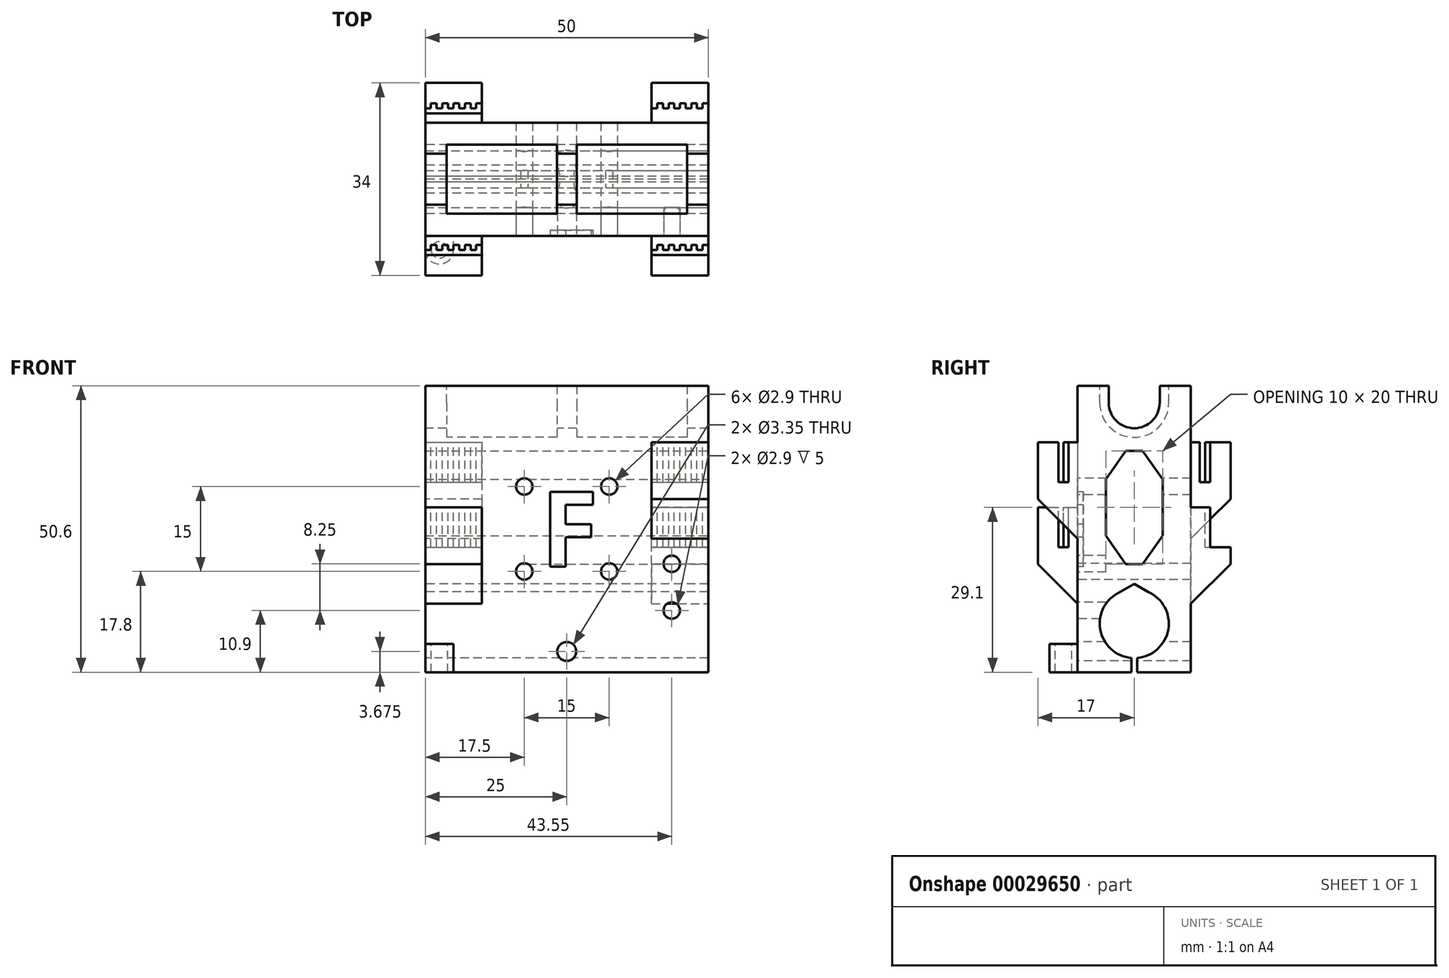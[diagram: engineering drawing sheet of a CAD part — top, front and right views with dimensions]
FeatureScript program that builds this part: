
annotation { "Feature Type Name" : "Feature", "Feature Type Description" : "" }
export const myFeature = defineFeature(function(context is Context, id is Id, definition is map)
    precondition{}
    {
        {
            var Q0;
            Q0=qCreatedBy(makeId("Top.planeOp"),FACE);
            var sketch = newSketch(context, id + "F0", { "sketchPlane" : qUnion([Q0])});
            skLineSegment(sketch, "E0.bottom", {"start": v(0, 0) * mm, "end": v(50, 0) * mm});
            skLineSegment(sketch, "E0.top", {"start": v(0, 20) * mm, "end": v(50, 20) * mm});
            skLineSegment(sketch, "E0.left", {"start": v(0, 0) * mm, "end": v(0, 20) * mm});
            skLineSegment(sketch, "E0.right", {"start": v(50, 0) * mm, "end": v(50, 20) * mm});
            skSolve(sketch);
        }
        {
            var Q0;
            Q0=qSketchRegion(id+"F0",true);
            extrude(context, id + "F1", {"entities" : qUnion([Q0]), "depth" : 50.6 * mm});
        }
        {
            var Q0;
            Q0=makeQuery(id+"F1.opExtrude","SWEPT_FACE",FACE,{"disambiguationData":[OSD([sQuery(id+"F0.wireOp",EDGE,"E0.left")])]});
            var sketch = newSketch(context, id + "F2", { "sketchPlane" : qUnion([Q0])});
            skCircle(sketch, "E1", {"center": v(-10, 8.6) * mm, "radius": 6.1 * mm});
            skCircle(sketch, "E2", {"center": v(-10, 47.6) * mm, "radius": 4.5 * mm});
            skLineSegment(sketch, "E3", {"start": v(-20, 47.6) * mm, "end": v(0, 47.6) * mm, "construction": true});
            skLineSegment(sketch, "E4", {"start": v(-14.5, 50.6) * mm, "end": v(-14.5, 47.6) * mm});
            skLineSegment(sketch, "E5", {"start": v(-5.5, 50.6) * mm, "end": v(-5.5, 47.6) * mm});
            skLineSegment(sketch, "E6", {"start": v(-20, 8.6) * mm, "end": v(0, 8.6) * mm, "construction": true});
            skLineSegment(sketch, "E7", {"start": v(-10, 8.6) * mm, "end": v(-10, 0) * mm, "construction": true});
            skLineSegment(sketch, "E8", {"start": v(-10, 0) * mm, "end": v(-10.5, 0) * mm});
            skLineSegment(sketch, "E9", {"start": v(-10.5, 0) * mm, "end": v(-10.5, 2.52) * mm});
            skLineSegment(sketch, "E10", {"start": v(-10.5, 2.52) * mm, "end": v(-9.5, 2.52) * mm});
            skLineSegment(sketch, "E11", {"start": v(-9.5, 2.52) * mm, "end": v(-9.5, 0) * mm});
            skLineSegment(sketch, "E12", {"start": v(-9.5, 0) * mm, "end": v(-10, 0) * mm});
            skLineSegment(sketch, "E13", {"start": v(-10, 14.7) * mm, "end": v(-10, 15.6) * mm});
            skLineSegment(sketch, "E14", {"start": v(-10, 15.6) * mm, "end": v(-6.39, 13.51) * mm});
            skLineSegment(sketch, "E15", {"start": v(-10, 15.6) * mm, "end": v(-13.61, 13.51) * mm});
            skCircle(sketch, "E16", {"center": v(-10, 47.6) * mm, "radius": 6.1 * mm});
            skLineSegment(sketch, "E17", {"start": v(-3.9, 47.6) * mm, "end": v(-3.9, 50.6) * mm});
            skLineSegment(sketch, "E18", {"start": v(-16.1, 47.6) * mm, "end": v(-16.1, 50.6) * mm});
            skSolve(sketch);
        }
        {
            var Q0;
            {var subQ0=sQuery(id+"F2.wireOp",EDGE,"E14");var subQ1=sQuery(id+"F2.wireOp",EDGE,"E1");var subQ3=makeQuery(id+"F2.imprint","INTERSECT",VERTEX,{"disambiguationData":[OD(0.0)],"derivedFrom":[subQ1,subQ0]});Q0=makeQuery(id+"F2.imprint","IMPRINT",FACE,{"disambiguationData":[TD([[makeQuery(id+"F2.imprint","IMPRINT",EDGE,{"disambiguationData":[TD([[subQ3,-1.0]])],"derivedFrom":subQ1}),1.0]])]});}
            var Q1;
            {var subQ0=sQuery(id+"F2.wireOp",EDGE,"E15");var subQ1=sQuery(id+"F2.wireOp",EDGE,"E1");var subQ3=makeQuery(id+"F2.imprint","INTERSECT",VERTEX,{"disambiguationData":[OD(0.0)],"derivedFrom":[subQ1,subQ0]});Q1=makeQuery(id+"F2.imprint","IMPRINT",FACE,{"disambiguationData":[TD([[makeQuery(id+"F2.imprint","IMPRINT",EDGE,{"disambiguationData":[TD([[subQ3,1.0]])],"derivedFrom":subQ1}),1.0]])]});}
            var Q2;
            Q2=makeQuery(id+"F2.imprint","IMPRINT",FACE,{"disambiguationData":[TD([[makeQuery(id+"F2.imprint","IMPRINT",EDGE,{"derivedFrom":sQuery(id+"F2.wireOp",EDGE,"E8")}),-1.0]])]});
            var Q3;
            {var subQ0=sQuery(id+"F2.wireOp",EDGE,"E10");Q3=makeQuery(id+"F2.imprint","IMPRINT",FACE,{"disambiguationData":[TD([[makeQuery(id+"F2.imprint","IMPRINT",EDGE,{"derivedFrom":subQ0}),-1.0]])]});}
            var Q4;
            {var subQ3=sQuery(id+"F2.wireOp",EDGE,"E13");Q4=makeQuery(id+"F2.imprint","IMPRINT",FACE,{"disambiguationData":[TD([[makeQuery(id+"F2.imprint","IMPRINT",EDGE,{"derivedFrom":subQ3}),-1.0]])]});}
            var Q5;
            {var subQ3=sQuery(id+"F2.wireOp",EDGE,"E13");Q5=makeQuery(id+"F2.imprint","IMPRINT",FACE,{"disambiguationData":[TD([[makeQuery(id+"F2.imprint","IMPRINT",EDGE,{"derivedFrom":subQ3}),1.0]])]});}
            var Q6;
            {var subQ7=sQuery(id+"F2.wireOp",EDGE,"E10");Q6=makeQuery(id+"F2.imprint","IMPRINT",FACE,{"disambiguationData":[TD([[makeQuery(id+"F2.imprint","IMPRINT",EDGE,{"derivedFrom":subQ7}),1.0]])]});}
            var Q7;
            {var subQ3=sQuery(id+"F2.wireOp",EDGE,"E5");Q7=makeQuery(id+"F2.imprint","IMPRINT",FACE,{"disambiguationData":[TD([[makeQuery(id+"F2.imprint","IMPRINT",EDGE,{"derivedFrom":subQ3}),-1.0]])]});}
            var Q8;
            {var subQ0=sQuery(id+"F2.wireOp",EDGE,"E4");Q8=makeQuery(id+"F2.imprint","IMPRINT",FACE,{"disambiguationData":[TD([[makeQuery(id+"F2.imprint","IMPRINT",EDGE,{"derivedFrom":subQ0}),1.0]])]});}
            var Q9;
            {var subQ0=sQuery(id+"F2.wireOp",EDGE,"E4");Q9=makeQuery(id+"F2.imprint","IMPRINT",FACE,{"disambiguationData":[TD([[makeQuery(id+"F2.imprint","IMPRINT",EDGE,{"derivedFrom":subQ0}),1.0]])]});}
            var Q10;
            {var subQ3=sQuery(id+"F2.wireOp",EDGE,"E5");Q10=makeQuery(id+"F2.imprint","IMPRINT",FACE,{"disambiguationData":[TD([[makeQuery(id+"F2.imprint","IMPRINT",EDGE,{"derivedFrom":subQ3}),-1.0]])]});}
            var Q11;
            {var subQ1=sQuery(id+"F2.wireOp",EDGE,"E2");var subQ4=makeQuery(id+"F2.imprint","INTERSECT",VERTEX,{"derivedFrom":[subQ1,sQuery(id+"F2.wireOp",EDGE,"E5")]});Q11=makeQuery(id+"F2.imprint","IMPRINT",FACE,{"disambiguationData":[TD([[makeQuery(id+"F2.imprint","IMPRINT",EDGE,{"disambiguationData":[TD([[subQ4,-1.0]])],"derivedFrom":subQ1}),1.0]])]});}
            extrude(context, id + "F3", {"entities" : qUnion([Q0, Q1, Q2, Q3, Q4, Q5, Q6, Q7, Q8, Q9, Q10, Q11]), "operationType" : NewBodyOperationType.REMOVE, "endBound" : BoundingType.THROUGH_ALL, "oppositeDirection" : true, "depth" : 25 * mm});
        }
        {
            var Q0;
            {var subQ3=sQuery(id+"F2.wireOp",EDGE,"E4");Q0=makeQuery(id+"F2.imprint","IMPRINT",FACE,{"disambiguationData":[TD([[makeQuery(id+"F2.imprint","IMPRINT",EDGE,{"derivedFrom":subQ3}),-1.0]])]});}
            var Q1;
            {var subQ3=sQuery(id+"F2.wireOp",EDGE,"E18");Q1=makeQuery(id+"F2.imprint","IMPRINT",FACE,{"disambiguationData":[TD([[makeQuery(id+"F2.imprint","IMPRINT",EDGE,{"derivedFrom":subQ3}),-1.0]])]});}
            var Q2;
            {var subQ3=sQuery(id+"F2.wireOp",EDGE,"E17");Q2=makeQuery(id+"F2.imprint","IMPRINT",FACE,{"disambiguationData":[TD([[makeQuery(id+"F2.imprint","IMPRINT",EDGE,{"derivedFrom":subQ3}),1.0]])]});}
            extrude(context, id + "F4", {"entities" : qUnion([Q0, Q1, Q2]), "operationType" : NewBodyOperationType.REMOVE, "oppositeDirection" : true, "depth" : 46.25 * mm});
        }
        {
            var Q0;
            {var subQ3=sQuery(id+"F2.wireOp",EDGE,"E4");Q0=makeQuery(id+"F2.imprint","IMPRINT",FACE,{"disambiguationData":[TD([[makeQuery(id+"F2.imprint","IMPRINT",EDGE,{"derivedFrom":subQ3}),-1.0]])]});}
            var Q1;
            {var subQ3=sQuery(id+"F2.wireOp",EDGE,"E18");Q1=makeQuery(id+"F2.imprint","IMPRINT",FACE,{"disambiguationData":[TD([[makeQuery(id+"F2.imprint","IMPRINT",EDGE,{"derivedFrom":subQ3}),-1.0]])]});}
            var Q2;
            {var subQ3=sQuery(id+"F2.wireOp",EDGE,"E17");Q2=makeQuery(id+"F2.imprint","IMPRINT",FACE,{"disambiguationData":[TD([[makeQuery(id+"F2.imprint","IMPRINT",EDGE,{"derivedFrom":subQ3}),1.0]])]});}
            extrude(context, id + "F5", {"entities" : qUnion([Q0, Q1, Q2]), "operationType" : NewBodyOperationType.ADD, "oppositeDirection" : true, "depth" : 26.75 * mm});
        }
        {
            var Q0;
            {var subQ3=sQuery(id+"F2.wireOp",EDGE,"E4");Q0=makeQuery(id+"F2.imprint","IMPRINT",FACE,{"disambiguationData":[TD([[makeQuery(id+"F2.imprint","IMPRINT",EDGE,{"derivedFrom":subQ3}),-1.0]])]});}
            var Q1;
            {var subQ3=sQuery(id+"F2.wireOp",EDGE,"E18");Q1=makeQuery(id+"F2.imprint","IMPRINT",FACE,{"disambiguationData":[TD([[makeQuery(id+"F2.imprint","IMPRINT",EDGE,{"derivedFrom":subQ3}),-1.0]])]});}
            var Q2;
            {var subQ3=sQuery(id+"F2.wireOp",EDGE,"E17");Q2=makeQuery(id+"F2.imprint","IMPRINT",FACE,{"disambiguationData":[TD([[makeQuery(id+"F2.imprint","IMPRINT",EDGE,{"derivedFrom":subQ3}),1.0]])]});}
            extrude(context, id + "F6", {"entities" : qUnion([Q0, Q1, Q2]), "operationType" : NewBodyOperationType.REMOVE, "oppositeDirection" : true, "depth" : 23.25 * mm});
        }
        {
            var Q0;
            {var subQ3=sQuery(id+"F2.wireOp",EDGE,"E4");Q0=makeQuery(id+"F2.imprint","IMPRINT",FACE,{"disambiguationData":[TD([[makeQuery(id+"F2.imprint","IMPRINT",EDGE,{"derivedFrom":subQ3}),-1.0]])]});}
            var Q1;
            {var subQ3=sQuery(id+"F2.wireOp",EDGE,"E18");Q1=makeQuery(id+"F2.imprint","IMPRINT",FACE,{"disambiguationData":[TD([[makeQuery(id+"F2.imprint","IMPRINT",EDGE,{"derivedFrom":subQ3}),-1.0]])]});}
            var Q2;
            {var subQ3=sQuery(id+"F2.wireOp",EDGE,"E17");Q2=makeQuery(id+"F2.imprint","IMPRINT",FACE,{"disambiguationData":[TD([[makeQuery(id+"F2.imprint","IMPRINT",EDGE,{"derivedFrom":subQ3}),1.0]])]});}
            extrude(context, id + "F7", {"entities" : qUnion([Q0, Q1, Q2]), "operationType" : NewBodyOperationType.ADD, "oppositeDirection" : true, "depth" : 3.75 * mm});
        }
        {
            var Q0;
            Q0=makeQuery(id+"F1.opExtrude","SWEPT_FACE",FACE,{"disambiguationData":[OSD([sQuery(id+"F0.wireOp",EDGE,"E0.bottom")])]});
            var sketch = newSketch(context, id + "F8", { "sketchPlane" : qUnion([Q0])});
            skLineSegment(sketch, "E19.bottom", {"start": v(0, 29.1) * mm, "end": v(10, 29.1) * mm});
            skLineSegment(sketch, "E19.top", {"start": v(0, 9.1) * mm, "end": v(10, 9.1) * mm});
            skLineSegment(sketch, "E19.left", {"start": v(0, 29.1) * mm, "end": v(0, 9.1) * mm});
            skLineSegment(sketch, "E19.right", {"start": v(10, 29.1) * mm, "end": v(10, 9.1) * mm});
            skLineSegment(sketch, "E20.bottom", {"start": v(50, 40.6) * mm, "end": v(40, 40.6) * mm});
            skLineSegment(sketch, "E20.top", {"start": v(50, 20.6) * mm, "end": v(40, 20.6) * mm});
            skLineSegment(sketch, "E20.left", {"start": v(50, 40.6) * mm, "end": v(50, 20.6) * mm});
            skLineSegment(sketch, "E20.right", {"start": v(40, 40.6) * mm, "end": v(40, 20.6) * mm});
            skPoint(sketch, "E21", {"position": v(0, 47.6) * mm});
            skPoint(sketch, "E22", {"position": v(0, 8.6) * mm});
            skSolve(sketch);
        }
        {
            var Q0;
            Q0=qSketchRegion(id+"F8",true);
            extrude(context, id + "F9", {"entities" : qUnion([Q0]), "operationType" : NewBodyOperationType.ADD, "depth" : 7 * mm});
        }
        {
            var Q0;
            Q0=makeQuery(id+"F9.opExtrude","CAP_EDGE",EDGE,{"disambiguationData":[OSD([sQuery(id+"F8.wireOp",EDGE,"E19.top")])],"isStart":false});
            var Q1;
            Q1=makeQuery(id+"F9.opExtrude","CAP_EDGE",EDGE,{"disambiguationData":[OSD([sQuery(id+"F8.wireOp",EDGE,"E20.top")])],"isStart":false});
            chamfer(context, id + "F10", {"entities" : qUnion([Q0, Q1]), "width" : 10 * mm, "tangentPropagation" : true});
        }
        {
            var Q0;
            Q0=makeQuery(id+"F9.opExtrude","SWEPT_FACE",FACE,{"disambiguationData":[OSD([sQuery(id+"F8.wireOp",EDGE,"E19.bottom")])]});
            var sketch = newSketch(context, id + "F11", { "sketchPlane" : qUnion([Q0])});
            skLineSegment(sketch, "E23", {"start": v(-935.9, 0) * mm, "end": v(-935.88, -4.54) * mm});
            skLineSegment(sketch, "E24.left", {"start": v(0, -3.4) * mm, "end": v(0, -1.6) * mm});
            skLineSegment(sketch, "E25", {"start": v(6, -2.5) * mm, "end": v(7, -2.5) * mm});
            skLineSegment(sketch, "E26", {"start": v(4, -2.5) * mm, "end": v(5, -2.5) * mm});
            skLineSegment(sketch, "E27", {"start": v(0, -2.5) * mm, "end": v(1, -2.5) * mm});
            skLineSegment(sketch, "E28", {"start": v(7, -1.6) * mm, "end": v(8, -1.6) * mm});
            skLineSegment(sketch, "E29", {"start": v(2, -2.5) * mm, "end": v(3, -2.5) * mm});
            skLineSegment(sketch, "E30", {"start": v(3, -1.6) * mm, "end": v(4, -1.6) * mm});
            skLineSegment(sketch, "E31", {"start": v(8, -2.5) * mm, "end": v(9, -2.5) * mm});
            skLineSegment(sketch, "E32", {"start": v(8, -1.6) * mm, "end": v(8, -2.5) * mm});
            skLineSegment(sketch, "E33", {"start": v(9, -2.5) * mm, "end": v(9, -1.6) * mm});
            skLineSegment(sketch, "E34", {"start": v(10, -1.6) * mm, "end": v(10, -2.5) * mm});
            skLineSegment(sketch, "E35", {"start": v(6, -1.6) * mm, "end": v(6, -2.5) * mm});
            skLineSegment(sketch, "E36", {"start": v(2, -1.6) * mm, "end": v(2, -2.5) * mm});
            skLineSegment(sketch, "E37", {"start": v(1, -1.6) * mm, "end": v(2, -1.6) * mm});
            skLineSegment(sketch, "E38", {"start": v(1, -2.5) * mm, "end": v(1, -1.6) * mm});
            skLineSegment(sketch, "E39", {"start": v(9, -1.6) * mm, "end": v(10, -1.6) * mm});
            skLineSegment(sketch, "E40", {"start": v(5, -1.6) * mm, "end": v(6, -1.6) * mm});
            skLineSegment(sketch, "E41", {"start": v(5, -2.5) * mm, "end": v(5, -1.6) * mm});
            skLineSegment(sketch, "E42", {"start": v(3, -2.5) * mm, "end": v(3, -1.6) * mm});
            skLineSegment(sketch, "E43", {"start": v(4, -1.6) * mm, "end": v(4, -2.5) * mm});
            skLineSegment(sketch, "E44", {"start": v(7, -2.5) * mm, "end": v(7, -1.6) * mm});
            skLineSegment(sketch, "E45", {"start": v(0, -1.6) * mm, "end": v(0, -2.5) * mm});
            skLineSegment(sketch, "E46", {"start": v(10, -2.5) * mm, "end": v(10, -3.4) * mm});
            skLineSegment(sketch, "E47", {"start": v(0, -3.4) * mm, "end": v(10, -3.4) * mm});
            skLineSegment(sketch, "E48", {"start": v(5.3, -1.6) * mm, "end": v(5.3, 0) * mm});
            skSolve(sketch);
        }
        {
            var Q0;
            Q0=qSketchRegion(id+"F11",true);
            extrude(context, id + "F12", {"entities" : qUnion([Q0]), "operationType" : NewBodyOperationType.REMOVE, "oppositeDirection" : true, "depth" : 7 * mm});
        }
        {
            var Q0;
            Q0=makeQuery(id+"F9.opExtrude","SWEPT_FACE",FACE,{"disambiguationData":[OSD([sQuery(id+"F8.wireOp",EDGE,"E20.bottom")])]});
            var sketch = newSketch(context, id + "F13", { "sketchPlane" : qUnion([Q0])});
            skLineSegment(sketch, "E49.left", {"start": v(40, -3.4) * mm, "end": v(40, -1.6) * mm});
            skLineSegment(sketch, "E50", {"start": v(46, -2.5) * mm, "end": v(47, -2.5) * mm});
            skLineSegment(sketch, "E51", {"start": v(44, -2.5) * mm, "end": v(45, -2.5) * mm});
            skLineSegment(sketch, "E52", {"start": v(40, -2.5) * mm, "end": v(41, -2.5) * mm});
            skLineSegment(sketch, "E53", {"start": v(47, -1.6) * mm, "end": v(48, -1.6) * mm});
            skLineSegment(sketch, "E54", {"start": v(42, -2.5) * mm, "end": v(43, -2.5) * mm});
            skLineSegment(sketch, "E55", {"start": v(43, -1.6) * mm, "end": v(44, -1.6) * mm});
            skLineSegment(sketch, "E56", {"start": v(48, -2.5) * mm, "end": v(49, -2.5) * mm});
            skLineSegment(sketch, "E57", {"start": v(48, -1.6) * mm, "end": v(48, -2.5) * mm});
            skLineSegment(sketch, "E58", {"start": v(49, -2.5) * mm, "end": v(49, -1.6) * mm});
            skLineSegment(sketch, "E59", {"start": v(50, -1.6) * mm, "end": v(50, -2.5) * mm});
            skLineSegment(sketch, "E60", {"start": v(46, -1.6) * mm, "end": v(46, -2.5) * mm});
            skLineSegment(sketch, "E61", {"start": v(42, -1.6) * mm, "end": v(42, -2.5) * mm});
            skLineSegment(sketch, "E62", {"start": v(41, -1.6) * mm, "end": v(42, -1.6) * mm});
            skLineSegment(sketch, "E63", {"start": v(41, -2.5) * mm, "end": v(41, -1.6) * mm});
            skLineSegment(sketch, "E64", {"start": v(49, -1.6) * mm, "end": v(50, -1.6) * mm});
            skLineSegment(sketch, "E65", {"start": v(45, -1.6) * mm, "end": v(46, -1.6) * mm});
            skLineSegment(sketch, "E66", {"start": v(45, -2.5) * mm, "end": v(45, -1.6) * mm});
            skLineSegment(sketch, "E67", {"start": v(43, -2.5) * mm, "end": v(43, -1.6) * mm});
            skLineSegment(sketch, "E68", {"start": v(44, -1.6) * mm, "end": v(44, -2.5) * mm});
            skLineSegment(sketch, "E69", {"start": v(47, -2.5) * mm, "end": v(47, -1.6) * mm});
            skLineSegment(sketch, "E70", {"start": v(40, -1.6) * mm, "end": v(40, -2.5) * mm});
            skLineSegment(sketch, "E71", {"start": v(50, -2.5) * mm, "end": v(50, -3.4) * mm});
            skLineSegment(sketch, "E72", {"start": v(40, -3.4) * mm, "end": v(50, -3.4) * mm});
            skLineSegment(sketch, "E73", {"start": v(45.23, -1.6) * mm, "end": v(45.23, 0) * mm});
            skSolve(sketch);
        }
        {
            var Q0;
            Q0=qSketchRegion(id+"F13",true);
            extrude(context, id + "F14", {"entities" : qUnion([Q0]), "operationType" : NewBodyOperationType.REMOVE, "oppositeDirection" : true, "depth" : 7 * mm});
        }
        {
            var Q0;
            Q0=makeQuery(id+"F1.opExtrude","SWEPT_FACE",FACE,{"disambiguationData":[OSD([sQuery(id+"F0.wireOp",EDGE,"E0.top")])]});
            var sketch = newSketch(context, id + "F15", { "sketchPlane" : qUnion([Q0])});
            skLineSegment(sketch, "E74.bottom", {"start": v(-50, 9.1) * mm, "end": v(-40, 9.1) * mm});
            skLineSegment(sketch, "E74.top", {"start": v(-50, 29.1) * mm, "end": v(-40, 29.1) * mm});
            skLineSegment(sketch, "E74.left", {"start": v(-50, 9.1) * mm, "end": v(-50, 29.1) * mm});
            skLineSegment(sketch, "E74.right", {"start": v(-40, 9.1) * mm, "end": v(-40, 29.1) * mm});
            skLineSegment(sketch, "E75.bottom", {"start": v(0, 40.6) * mm, "end": v(-10, 40.6) * mm});
            skLineSegment(sketch, "E75.top", {"start": v(0, 20.6) * mm, "end": v(-10, 20.6) * mm});
            skLineSegment(sketch, "E75.left", {"start": v(0, 40.6) * mm, "end": v(0, 20.6) * mm});
            skLineSegment(sketch, "E75.right", {"start": v(-10, 40.6) * mm, "end": v(-10, 20.6) * mm});
            skSolve(sketch);
        }
        {
            var Q0;
            Q0=qSketchRegion(id+"F15",true);
            extrude(context, id + "F16", {"entities" : qUnion([Q0]), "operationType" : NewBodyOperationType.ADD, "depth" : 7 * mm});
        }
        {
            var Q0;
            Q0=makeQuery(id+"F16.opExtrude","SWEPT_FACE",FACE,{"disambiguationData":[OSD([sQuery(id+"F15.wireOp",EDGE,"E74.top")])]});
            var sketch = newSketch(context, id + "F17", { "sketchPlane" : qUnion([Q0])});
            skLineSegment(sketch, "E76.left", {"start": v(40, 21.6) * mm, "end": v(40, 23.4) * mm});
            skLineSegment(sketch, "E77", {"start": v(46, 22.5) * mm, "end": v(47, 22.5) * mm});
            skLineSegment(sketch, "E78", {"start": v(44, 22.5) * mm, "end": v(45, 22.5) * mm});
            skLineSegment(sketch, "E79", {"start": v(40, 22.5) * mm, "end": v(41, 22.5) * mm});
            skLineSegment(sketch, "E80", {"start": v(47, 23.4) * mm, "end": v(48, 23.4) * mm});
            skLineSegment(sketch, "E81", {"start": v(42, 22.5) * mm, "end": v(43, 22.5) * mm});
            skLineSegment(sketch, "E82", {"start": v(43, 23.4) * mm, "end": v(44, 23.4) * mm});
            skLineSegment(sketch, "E83", {"start": v(48, 22.5) * mm, "end": v(49, 22.5) * mm});
            skLineSegment(sketch, "E84", {"start": v(48, 23.4) * mm, "end": v(48, 22.5) * mm});
            skLineSegment(sketch, "E85", {"start": v(49, 22.5) * mm, "end": v(49, 23.4) * mm});
            skLineSegment(sketch, "E86", {"start": v(50, 23.4) * mm, "end": v(50, 22.5) * mm});
            skLineSegment(sketch, "E87", {"start": v(46, 23.4) * mm, "end": v(46, 22.5) * mm});
            skLineSegment(sketch, "E88", {"start": v(42, 23.4) * mm, "end": v(42, 22.5) * mm});
            skLineSegment(sketch, "E89", {"start": v(41, 23.4) * mm, "end": v(42, 23.4) * mm});
            skLineSegment(sketch, "E90", {"start": v(41, 22.5) * mm, "end": v(41, 23.4) * mm});
            skLineSegment(sketch, "E91", {"start": v(49, 23.4) * mm, "end": v(50, 23.4) * mm});
            skLineSegment(sketch, "E92", {"start": v(45, 23.4) * mm, "end": v(46, 23.4) * mm});
            skLineSegment(sketch, "E93", {"start": v(45, 22.5) * mm, "end": v(45, 23.4) * mm});
            skLineSegment(sketch, "E94", {"start": v(43, 22.5) * mm, "end": v(43, 23.4) * mm});
            skLineSegment(sketch, "E95", {"start": v(44, 23.4) * mm, "end": v(44, 22.5) * mm});
            skLineSegment(sketch, "E96", {"start": v(47, 22.5) * mm, "end": v(47, 23.4) * mm});
            skLineSegment(sketch, "E97", {"start": v(40, 23.4) * mm, "end": v(40, 22.5) * mm});
            skLineSegment(sketch, "E98", {"start": v(50, 22.5) * mm, "end": v(50, 21.6) * mm});
            skLineSegment(sketch, "E99", {"start": v(40, 21.6) * mm, "end": v(50, 21.6) * mm});
            skLineSegment(sketch, "E100", {"start": v(45, 21.6) * mm, "end": v(45, 20) * mm});
            skSolve(sketch);
        }
        {
            var Q0;
            {var subQ4=sQuery(id+"F17.wireOp",EDGE,"E76.left");Q0=makeQuery(id+"F17.imprint","IMPRINT",FACE,{"disambiguationData":[TD([[makeQuery(id+"F17.imprint","IMPRINT",EDGE,{"derivedFrom":subQ4}),1.0]])]});}
            extrude(context, id + "F18", {"entities" : qUnion([Q0]), "operationType" : NewBodyOperationType.REMOVE, "oppositeDirection" : true, "depth" : 7 * mm});
        }
        {
            var Q0;
            Q0=makeQuery(id+"F16.opExtrude","SWEPT_FACE",FACE,{"disambiguationData":[OSD([sQuery(id+"F15.wireOp",EDGE,"E75.bottom")])]});
            var sketch = newSketch(context, id + "F19", { "sketchPlane" : qUnion([Q0])});
            skLineSegment(sketch, "E101", {"start": v(6, 22.5) * mm, "end": v(7, 22.5) * mm});
            skLineSegment(sketch, "E102", {"start": v(4, 22.5) * mm, "end": v(5, 22.5) * mm});
            skLineSegment(sketch, "E103", {"start": v(0, 22.5) * mm, "end": v(1, 22.5) * mm});
            skLineSegment(sketch, "E104", {"start": v(7, 23.4) * mm, "end": v(8, 23.4) * mm});
            skLineSegment(sketch, "E105", {"start": v(2, 22.5) * mm, "end": v(3, 22.5) * mm});
            skLineSegment(sketch, "E106", {"start": v(3, 23.4) * mm, "end": v(4, 23.4) * mm});
            skLineSegment(sketch, "E107", {"start": v(8, 22.5) * mm, "end": v(9, 22.5) * mm});
            skLineSegment(sketch, "E108", {"start": v(8, 23.4) * mm, "end": v(8, 22.5) * mm});
            skLineSegment(sketch, "E109", {"start": v(9, 22.5) * mm, "end": v(9, 23.4) * mm});
            skLineSegment(sketch, "E110", {"start": v(10, 23.4) * mm, "end": v(10, 22.5) * mm});
            skLineSegment(sketch, "E111", {"start": v(6, 23.4) * mm, "end": v(6, 22.5) * mm});
            skLineSegment(sketch, "E112", {"start": v(2, 23.4) * mm, "end": v(2, 22.5) * mm});
            skLineSegment(sketch, "E113", {"start": v(1, 23.4) * mm, "end": v(2, 23.4) * mm});
            skLineSegment(sketch, "E114", {"start": v(1, 22.5) * mm, "end": v(1, 23.4) * mm});
            skLineSegment(sketch, "E115", {"start": v(9, 23.4) * mm, "end": v(10, 23.4) * mm});
            skLineSegment(sketch, "E116", {"start": v(5, 23.4) * mm, "end": v(6, 23.4) * mm});
            skLineSegment(sketch, "E117", {"start": v(5, 22.5) * mm, "end": v(5, 23.4) * mm});
            skLineSegment(sketch, "E118", {"start": v(3, 22.5) * mm, "end": v(3, 23.4) * mm});
            skLineSegment(sketch, "E119", {"start": v(4, 23.4) * mm, "end": v(4, 22.5) * mm});
            skLineSegment(sketch, "E120", {"start": v(7, 22.5) * mm, "end": v(7, 23.4) * mm});
            skLineSegment(sketch, "E121", {"start": v(10, 22.5) * mm, "end": v(10, 21.6) * mm});
            skLineSegment(sketch, "E122", {"start": v(0, 21.6) * mm, "end": v(10, 21.6) * mm});
            skLineSegment(sketch, "E123", {"start": v(5, 21.6) * mm, "end": v(5, 20) * mm});
            skLineSegment(sketch, "E124", {"start": v(0, 21.6) * mm, "end": v(0, 22.5) * mm});
            skSolve(sketch);
        }
        {
            var Q0;
            Q0=makeQuery(id+"F19.imprint","IMPRINT",FACE,{"disambiguationData":[TD([[makeQuery(id+"F19.imprint","IMPRINT",EDGE,{"derivedFrom":sQuery(id+"F19.wireOp",EDGE,"E101")}),-1.0]])]});
            extrude(context, id + "F20", {"entities" : qUnion([Q0]), "operationType" : NewBodyOperationType.REMOVE, "oppositeDirection" : true, "depth" : 7 * mm});
        }
        {
            var Q0;
            Q0=makeQuery(id+"F16.opExtrude","CAP_EDGE",EDGE,{"disambiguationData":[OSD([sQuery(id+"F15.wireOp",EDGE,"E75.top")])],"isStart":false});
            var Q1;
            Q1=makeQuery(id+"F16.opExtrude","CAP_EDGE",EDGE,{"disambiguationData":[OSD([sQuery(id+"F15.wireOp",EDGE,"E74.bottom")])],"isStart":false});
            chamfer(context, id + "F21", {"entities" : qUnion([Q0, Q1]), "width" : 10 * mm, "tangentPropagation" : true});
        }
        {
            var Q0;
            Q0=makeQuery(id+"F1.opExtrude","SWEPT_FACE",FACE,{"disambiguationData":[OSD([sQuery(id+"F0.wireOp",EDGE,"E0.bottom")])]});
            var sketch = newSketch(context, id + "F22", { "sketchPlane" : qUnion([Q0])});
            skCircle(sketch, "E125", {"center": v(17.5, 32.8) * mm, "radius": 1.45 * mm});
            skCircle(sketch, "E126", {"center": v(32.5, 32.8) * mm, "radius": 1.45 * mm});
            skCircle(sketch, "E127", {"center": v(17.5, 17.8) * mm, "radius": 1.45 * mm});
            skCircle(sketch, "E128", {"center": v(32.5, 17.8) * mm, "radius": 1.45 * mm});
            skLineSegment(sketch, "E129", {"start": v(17.5, 32.8) * mm, "end": v(0, 32.8) * mm});
            skLineSegment(sketch, "E130", {"start": v(32.5, 17.8) * mm, "end": v(50, 17.8) * mm});
            skLineSegment(sketch, "E131", {"start": v(32.5, 32.8) * mm, "end": v(32.5, 50.6) * mm});
            skLineSegment(sketch, "E132", {"start": v(17.5, 17.8) * mm, "end": v(17.5, 0) * mm});
            skCircle(sketch, "E133", {"center": v(25, 3.68) * mm, "radius": 1.68 * mm});
            skLineSegment(sketch, "E134", {"start": v(25, 0) * mm, "end": v(25, 13.82) * mm, "construction": true});
            skSolve(sketch);
        }
        {
            var Q0;
            Q0=qSketchRegion(id+"F22",true);
            var Q1;
            Q1=makeQuery(id+"F22.imprint","IMPRINT",FACE,{"disambiguationData":[TD([[makeQuery(id+"F22.imprint","IMPRINT",EDGE,{"derivedFrom":sQuery(id+"F22.wireOp",EDGE,"E125")}),1.0]])]});
            var Q2;
            Q2=makeQuery(id+"F22.imprint","IMPRINT",FACE,{"disambiguationData":[TD([[makeQuery(id+"F22.imprint","IMPRINT",EDGE,{"derivedFrom":sQuery(id+"F22.wireOp",EDGE,"E126")}),1.0]])]});
            var Q3;
            Q3=makeQuery(id+"F22.imprint","IMPRINT",FACE,{"disambiguationData":[TD([[makeQuery(id+"F22.imprint","IMPRINT",EDGE,{"derivedFrom":sQuery(id+"F22.wireOp",EDGE,"E128")}),1.0]])]});
            var Q4;
            Q4=makeQuery(id+"F22.imprint","IMPRINT",FACE,{"disambiguationData":[TD([[makeQuery(id+"F22.imprint","IMPRINT",EDGE,{"derivedFrom":sQuery(id+"F22.wireOp",EDGE,"E127")}),1.0]])]});
            extrude(context, id + "F23", {"entities" : qUnion([Q0, Q1, Q2, Q3, Q4]), "operationType" : NewBodyOperationType.REMOVE, "endBound" : BoundingType.THROUGH_ALL, "oppositeDirection" : true, "depth" : 25 * mm});
        }
        {
            var Q0;
            Q0=makeQuery(id+"F1.opExtrude","SWEPT_FACE",FACE,{"disambiguationData":[OSD([sQuery(id+"F0.wireOp",EDGE,"E0.bottom")])]});
            var sketch = newSketch(context, id + "F24", { "sketchPlane" : qUnion([Q0])});
            skCircle(sketch, "E135", {"center": v(43.55, 19.15) * mm, "radius": 1.45 * mm});
            skCircle(sketch, "E136", {"center": v(43.55, 10.9) * mm, "radius": 1.45 * mm});
            skSolve(sketch);
        }
        {
            var Q0;
            Q0=qSketchRegion(id+"F24",true);
            extrude(context, id + "F25", {"entities" : qUnion([Q0]), "operationType" : NewBodyOperationType.REMOVE, "oppositeDirection" : true, "depth" : 5 * mm});
        }
        {
            var Q0;
            Q0=makeQuery(id+"F1.opExtrude","SWEPT_FACE",FACE,{"disambiguationData":[OSD([sQuery(id+"F0.wireOp",EDGE,"E0.bottom")])]});
            var sketch = newSketch(context, id + "F26", { "sketchPlane" : qUnion([Q0])});
            skText(sketch, "E137", { "text": "F", "fontName": "OpenSans-Bold.ttf"});
            skLineSegment(sketch, "E138", {"start": v(17.5, 32.8) * mm, "end": v(17.5, 17.8) * mm, "construction": true});
            skLineSegment(sketch, "E139", {"start": v(17.5, 17.8) * mm, "end": v(32.5, 17.8) * mm, "construction": true});
            skLineSegment(sketch, "E140", {"start": v(32.5, 17.8) * mm, "end": v(32.5, 32.8) * mm, "construction": true});
            skLineSegment(sketch, "E141", {"start": v(32.5, 32.8) * mm, "end": v(17.5, 32.8) * mm, "construction": true});
            skLineSegment(sketch, "E142", {"start": v(17.5, 25.3) * mm, "end": v(20.4, 25.3) * mm, "construction": true});
            skLineSegment(sketch, "E143", {"start": v(29.6, 25.3) * mm, "end": v(32.5, 25.3) * mm, "construction": true});
            skLineSegment(sketch, "E144", {"start": v(25, 18.66) * mm, "end": v(25, 17.8) * mm, "construction": true});
            skLineSegment(sketch, "E145", {"start": v(25, 32.8) * mm, "end": v(25, 31.94) * mm, "construction": true});
            const initialGuessF26  = {"E137": [0.0204, 0.01866, 1, 0, 0.01328]};
            skSetInitialGuess(sketch, initialGuessF26);
            skSolve(sketch);
        }
        {
            var Q0;
            Q0=qSketchRegion(id+"F26",true);
            extrude(context, id + "F27", {"entities" : qUnion([Q0]), "operationType" : NewBodyOperationType.REMOVE, "oppositeDirection" : true, "depth" : 1 * mm});
        }
        {
            var Q0;
            Q0=makeQuery(id+"F1.opExtrude","SWEPT_FACE",FACE,{"disambiguationData":[OSD([sQuery(id+"F0.wireOp",EDGE,"E0.bottom")])]});
            var sketch = newSketch(context, id + "F28", { "sketchPlane" : qUnion([Q0])});
            skLineSegment(sketch, "E146.bottom", {"start": v(0, 0) * mm, "end": v(5, 0) * mm});
            skLineSegment(sketch, "E146.top", {"start": v(0, 5) * mm, "end": v(5, 5) * mm});
            skLineSegment(sketch, "E146.left", {"start": v(0, 0) * mm, "end": v(0, 5) * mm});
            skLineSegment(sketch, "E146.right", {"start": v(5, 0) * mm, "end": v(5, 5) * mm});
            skSolve(sketch);
        }
        {
            var Q0;
            Q0=qSketchRegion(id+"F28",true);
            extrude(context, id + "F29", {"entities" : qUnion([Q0]), "operationType" : NewBodyOperationType.ADD, "depth" : 5 * mm});
        }
        {
            var Q0;
            Q0=makeQuery(id+"F29.opExtrude","SWEPT_FACE",FACE,{"disambiguationData":[OSD([sQuery(id+"F28.wireOp",EDGE,"E146.top")])]});
            var sketch = newSketch(context, id + "F30", { "sketchPlane" : qUnion([Q0])});
            skCircle(sketch, "E147", {"center": v(2.5, -2.5) * mm, "radius": 1.45 * mm});
            skLineSegment(sketch, "E148", {"start": v(0, -2.5) * mm, "end": v(5, -2.5) * mm});
            skSolve(sketch);
        }
        {
            var Q0;
            Q0=qSketchRegion(id+"F30",true);
            extrude(context, id + "F31", {"entities" : qUnion([Q0]), "operationType" : NewBodyOperationType.REMOVE, "oppositeDirection" : true, "depth" : 25 * mm});
        }
        {
            var Q0;
            Q0=makeQuery(id+"F29.opExtrude","CAP_EDGE",EDGE,{"disambiguationData":[OSD([sQuery(id+"F28.wireOp",EDGE,"E146.left")])],"isStart":false});
            var Q1;
            Q1=makeQuery(id+"F29.opExtrude","CAP_EDGE",EDGE,{"disambiguationData":[OSD([sQuery(id+"F28.wireOp",EDGE,"E146.right")])],"isStart":false});
            fillet(context, id + "F32", {"entities" : qUnion([Q0, Q1]), "radius" : 2.5 * mm, "tangentPropagation" : true, "allowEdgeOverflow" : false});
        }
        {
            var Q0;
            Q0=makeQuery(id+"F16.boolean.opBoolean","MERGE",FACE,{"derivedFrom":[makeQuery(id+"F9.boolean.opBoolean","MERGE",FACE,{"derivedFrom":[makeQuery(id+"F1.opExtrude","SWEPT_FACE",FACE,{"disambiguationData":[OSD([sQuery(id+"F0.wireOp",EDGE,"E0.right")])]}),makeQuery(id+"F9.opExtrude","SWEPT_FACE",FACE,{"disambiguationData":[OSD([sQuery(id+"F8.wireOp",EDGE,"E20.left")])]})]}),makeQuery(id+"F16.opExtrude","SWEPT_FACE",FACE,{"disambiguationData":[OSD([sQuery(id+"F15.wireOp",EDGE,"E74.left")])]})]});
            var sketch = newSketch(context, id + "F33", { "sketchPlane" : qUnion([Q0])});
            skLineSegment(sketch, "E149.bottom", {"start": v(15, 34.1) * mm, "end": v(5, 34.1) * mm, "construction": true});
            skLineSegment(sketch, "E149.top", {"start": v(15, 24.1) * mm, "end": v(5, 24.1) * mm, "construction": true});
            skLineSegment(sketch, "E149.left", {"start": v(15, 34.1) * mm, "end": v(15, 24.1) * mm});
            skLineSegment(sketch, "E149.right", {"start": v(5, 34.1) * mm, "end": v(5, 24.1) * mm});
            skPoint(sketch, "E149.middle", {"position": v(10, 29.1) * mm});
            skPoint(sketch, "E149.middle.positionSnap0", {"position": v(10, 43.1) * mm});
            skPoint(sketch, "E149.centerSnap0", {"position": v(10, 43.1) * mm});
            skLineSegment(sketch, "E150.bottom", {"start": v(11.5, 39.1) * mm, "end": v(8.5, 39.1) * mm});
            skLineSegment(sketch, "E150.top", {"start": v(11.5, 19.1) * mm, "end": v(8.5, 19.1) * mm});
            skLineSegment(sketch, "E150.left", {"start": v(11.5, 39.1) * mm, "end": v(11.5, 19.1) * mm, "construction": true});
            skLineSegment(sketch, "E150.right", {"start": v(8.5, 39.1) * mm, "end": v(8.5, 19.1) * mm, "construction": true});
            skLineSegment(sketch, "E151", {"start": v(5, 24.1) * mm, "end": v(8.5, 19.1) * mm});
            skLineSegment(sketch, "E152", {"start": v(11.5, 19.1) * mm, "end": v(15, 24.1) * mm});
            skLineSegment(sketch, "E153", {"start": v(15, 34.1) * mm, "end": v(11.5, 39.1) * mm});
            skLineSegment(sketch, "E154", {"start": v(5, 34.1) * mm, "end": v(8.5, 39.1) * mm});
            skSolve(sketch);
        }
        {
            var Q0;
            Q0 = qSketchRegion(id + "F33", true);
            extrude(context, id + "F34", {"entities" : qUnion([Q0]), "operationType" : NewBodyOperationType.REMOVE, "endBound" : BoundingType.THROUGH_ALL, "oppositeDirection" : true, "depth" : 25 * mm});
        }
    });
